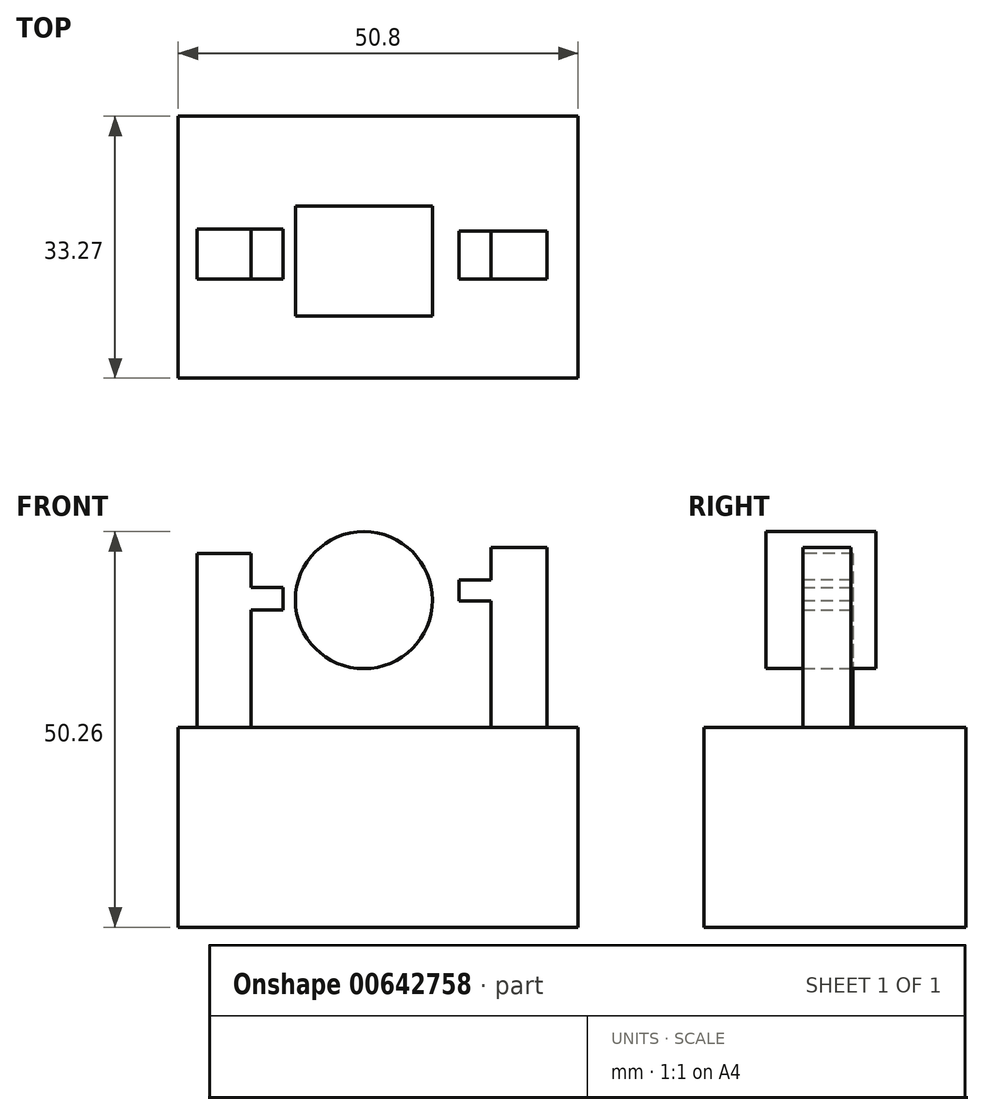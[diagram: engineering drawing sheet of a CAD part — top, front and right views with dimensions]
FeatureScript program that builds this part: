
annotation { "Feature Type Name" : "Feature", "Feature Type Description" : "" }
export const myFeature = defineFeature(function(context is Context, id is Id, definition is map)
    precondition{}
    {
        {
            var Q0;
            Q0=qCreatedBy(makeId("Front.planeOp"),FACE);
            var sketch = newSketch(context, id + "F0", { "sketchPlane" : qUnion([Q0])});
            skLineSegment(sketch, "E0.bottom", {"start": v(0, 0) * mm, "end": v(50.8, 0) * mm});
            skLineSegment(sketch, "E0.top", {"start": v(0, 25.4) * mm, "end": v(50.8, 25.4) * mm});
            skLineSegment(sketch, "E0.left", {"start": v(0, 0) * mm, "end": v(0, 25.4) * mm});
            skLineSegment(sketch, "E0.right", {"start": v(50.8, 0) * mm, "end": v(50.8, 25.4) * mm});
            skSolve(sketch);
        }
        {
            var Q0;
            Q0=makeQuery(id+"F0.imprint","IMPRINT",FACE,{"disambiguationData":[TD([[makeQuery(id+"F0.imprint","IMPRINT",EDGE,{"derivedFrom":sQuery(id+"F0.wireOp",EDGE,"E0.bottom")}),1.0]])]});
            extrude(context, id + "F1", {"entities" : qUnion([Q0]), "depth" : 45.72 * mm, "offsetDistance" : 25.4 * mm});
        }
        {
            var Q0;
            Q0=makeQuery(id+"F1.opExtrude","SWEPT_FACE",FACE,{"disambiguationData":[OSD([sQuery(id+"F0.wireOp",EDGE,"E0.top")])]});
            var sketch = newSketch(context, id + "F2", { "sketchPlane" : qUnion([Q0])});
            skLineSegment(sketch, "E1.bottom", {"start": v(2.41, -14.35) * mm, "end": v(9.27, -14.35) * mm});
            skLineSegment(sketch, "E1.top", {"start": v(2.41, -20.7) * mm, "end": v(9.27, -20.7) * mm});
            skLineSegment(sketch, "E1.left", {"start": v(2.41, -14.35) * mm, "end": v(2.41, -20.7) * mm});
            skLineSegment(sketch, "E1.right", {"start": v(9.27, -14.35) * mm, "end": v(9.27, -20.7) * mm});
            skLineSegment(sketch, "E2.bottom", {"start": v(39.75, -20.7) * mm, "end": v(45.85, -20.7) * mm});
            skLineSegment(sketch, "E2.top", {"start": v(39.75, -13.84) * mm, "end": v(45.85, -13.84) * mm});
            skLineSegment(sketch, "E2.left", {"start": v(39.75, -20.7) * mm, "end": v(39.75, -13.84) * mm});
            skLineSegment(sketch, "E2.right", {"start": v(45.85, -20.7) * mm, "end": v(45.85, -13.84) * mm});
            skSolve(sketch);
        }
        {
            var Q0;
            Q0=makeQuery(id+"F2.imprint","IMPRINT",FACE,{"disambiguationData":[TD([[makeQuery(id+"F2.imprint","IMPRINT",EDGE,{"derivedFrom":sQuery(id+"F2.wireOp",EDGE,"E1.bottom")}),-1.0]])]});
            extrude(context, id + "F3", {"entities" : qUnion([Q0]), "operationType" : NewBodyOperationType.ADD, "depth" : 22.1 * mm, "offsetDistance" : 25.4 * mm});
        }
        {
            var Q0;
            Q0=makeQuery(id+"F1.opExtrude","SWEPT_FACE",FACE,{"disambiguationData":[OSD([sQuery(id+"F0.wireOp",EDGE,"E0.top")])]});
            var sketch = newSketch(context, id + "F4", { "sketchPlane" : qUnion([Q0])});
            skLineSegment(sketch, "E3.bottom", {"start": v(39.75, -20.7) * mm, "end": v(46.86, -20.7) * mm});
            skLineSegment(sketch, "E3.top", {"start": v(39.75, -14.6) * mm, "end": v(46.86, -14.6) * mm});
            skLineSegment(sketch, "E3.left", {"start": v(39.75, -20.7) * mm, "end": v(39.75, -14.6) * mm});
            skLineSegment(sketch, "E3.right", {"start": v(46.86, -20.7) * mm, "end": v(46.86, -14.6) * mm});
            skSolve(sketch);
        }
        {
            var Q0;
            Q0=makeQuery(id+"F4.imprint","IMPRINT",FACE,{"disambiguationData":[TD([[makeQuery(id+"F4.imprint","IMPRINT",EDGE,{"derivedFrom":sQuery(id+"F4.wireOp",EDGE,"E3.bottom")}),1.0]])]});
            extrude(context, id + "F5", {"entities" : qUnion([Q0]), "operationType" : NewBodyOperationType.ADD, "depth" : 22.86 * mm, "offsetDistance" : 25.4 * mm});
        }
        {
            var Q0;
            Q0=makeQuery(id+"F5.opExtrude","SWEPT_FACE",FACE,{"disambiguationData":[OSD([sQuery(id+"F4.wireOp",EDGE,"E3.left")])]});
            var sketch = newSketch(context, id + "F6", { "sketchPlane" : qUnion([Q0])});
            skLineSegment(sketch, "E4.bottom", {"start": v(14.6, 44.13) * mm, "end": v(20.7, 44.13) * mm});
            skLineSegment(sketch, "E4.top", {"start": v(14.6, 41.45) * mm, "end": v(20.7, 41.45) * mm});
            skLineSegment(sketch, "E4.left", {"start": v(14.6, 44.13) * mm, "end": v(14.6, 41.45) * mm});
            skLineSegment(sketch, "E4.right", {"start": v(20.7, 44.13) * mm, "end": v(20.7, 41.45) * mm});
            skSolve(sketch);
        }
        {
            var Q0;
            Q0=makeQuery(id+"F6.imprint","IMPRINT",FACE,{"disambiguationData":[TD([[makeQuery(id+"F6.imprint","IMPRINT",EDGE,{"derivedFrom":sQuery(id+"F6.wireOp",EDGE,"E4.bottom")}),-1.0]])]});
            extrude(context, id + "F7", {"entities" : qUnion([Q0]), "operationType" : NewBodyOperationType.ADD, "depth" : 4.06 * mm, "offsetDistance" : 25.4 * mm});
        }
        {
            var Q0;
            Q0=makeQuery(id+"F3.opExtrude","SWEPT_FACE",FACE,{"disambiguationData":[OSD([sQuery(id+"F2.wireOp",EDGE,"E1.right")])]});
            var sketch = newSketch(context, id + "F8", { "sketchPlane" : qUnion([Q0])});
            skLineSegment(sketch, "E5.bottom", {"start": v(-20.7, 43.15) * mm, "end": v(-14.35, 43.15) * mm});
            skLineSegment(sketch, "E5.top", {"start": v(-20.7, 40.33) * mm, "end": v(-14.35, 40.33) * mm});
            skLineSegment(sketch, "E5.left", {"start": v(-20.7, 43.15) * mm, "end": v(-20.7, 40.33) * mm});
            skLineSegment(sketch, "E5.right", {"start": v(-14.35, 43.15) * mm, "end": v(-14.35, 40.33) * mm});
            skSolve(sketch);
        }
        {
            var Q0;
            Q0=makeQuery(id+"F8.imprint","IMPRINT",FACE,{"disambiguationData":[TD([[makeQuery(id+"F8.imprint","IMPRINT",EDGE,{"derivedFrom":sQuery(id+"F8.wireOp",EDGE,"E5.bottom")}),-1.0]])]});
            extrude(context, id + "F9", {"entities" : qUnion([Q0]), "operationType" : NewBodyOperationType.ADD, "depth" : 4.06 * mm, "offsetDistance" : 25.4 * mm});
        }
        {
            var Q0;
            Q0=qCreatedBy(makeId("Front.planeOp"),FACE);
            var sketch = newSketch(context, id + "F10", { "sketchPlane" : qUnion([Q0])});
            skCircle(sketch, "E6", {"center": v(23.58, 41.56) * mm, "radius": 8.7 * mm});
            skSolve(sketch);
        }
        {
            var Q0;
            Q0=makeQuery(id+"F10.imprint","IMPRINT",FACE,{"disambiguationData":[TD([[makeQuery(id+"F10.imprint","IMPRINT",EDGE,{"derivedFrom":sQuery(id+"F10.wireOp",EDGE,"E6")}),1.0]])]});
            var Q1;
            Q1=sQuery(id+"F10.wireOp",EDGE,"E6");
            extrude(context, id + "F11", {"entities" : qUnion([Q0]), "surfaceEntities" : qUnion([Q1]), "depth" : 25.4 * mm, "offsetDistance" : 25.4 * mm});
        }
        {
            var Q0;
            Q0=makeQuery(id+"F11.opExtrude","CAP_FACE",FACE,{"disambiguationData":[OSD([sQuery(id+"F10.wireOp",EDGE,"E6")])],"isStart":true});
            extrude(context, id + "F12", {"entities" : qUnion([Q0]), "operationType" : NewBodyOperationType.REMOVE, "oppositeDirection" : true, "depth" : 11.43 * mm, "offsetDistance" : 25.4 * mm});
        }
        {
            var Q0;
            Q0=makeQuery(id+"F1.opExtrude","CAP_FACE",FACE,{"disambiguationData":[OSD([sQuery(id+"F0.wireOp",EDGE,"E0.bottom"),sQuery(id+"F0.wireOp",EDGE,"E0.top"),sQuery(id+"F0.wireOp",EDGE,"E0.left"),sQuery(id+"F0.wireOp",EDGE,"E0.right")])],"isStart":false});
            extrude(context, id + "F13", {"entities" : qUnion([Q0]), "operationType" : NewBodyOperationType.REMOVE, "oppositeDirection" : true, "depth" : 12.45 * mm, "offsetDistance" : 25.4 * mm});
        }
    });
